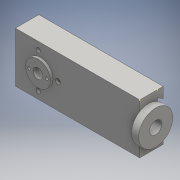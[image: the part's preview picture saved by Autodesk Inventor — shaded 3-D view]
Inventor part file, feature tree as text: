
AUTODESK INVENTOR PART (.ipt)
format: ipt  version: 2016 (Build 200138000, 138)  size: 212,480 bytes
history: native  units: mm
features: sketch x12, extrude x10
ambient origin geometry x8: Origin, YZ Plane, XZ Plane, XY Plane, X Axis, Y Axis, Z Axis, Center Point
bodies: Solid1 (feature_tree)
feature tree (22):
  extrude  "Extrusion1"  Depth=41.4mm
  extrude  "Extrusion2"  Depth=220.0mm
  extrude  "Extrusion3"  Depth=10.2mm
  sketch  "Sketch4"  dims[d7=65.0mm d8=19.0mm]
  extrude  "Extrusion4"  Depth=19.0mm
  sketch  "Sketch6"  dims[d13=15.1mm d14=141.9mm]
  extrude  "Extrusion5"  Depth=15.1mm
  extrude  "Extrusion6"  Depth=141.9mm
  extrude  "Extrusion7"  Depth=26.9mm
  extrude  "Extrusion8"  Depth=4.6mm
  extrude  "Extrusion9"  Depth=11.0mm TaperAngle=0.0deg
  extrude  "Extrusion10"  Depth=12.7mm TaperAngle=0.0deg
  sketch  "Sketch1"  dims[d0=89.0mm d1=41.4mm]
  sketch  "Sketch2"  dims[d2=220.0mm d3=0.0mm d4=18.6mm]
  sketch  "Sketch3"  dims[d5=10.2mm d6=12.5mm]
  sketch  "Sketch5"  dims[d9=301.25mm d10=0.0mm d12=15.1mm]
  sketch  "Sketch7"  dims[d15=26.9mm d16=0.0mm d17=28.6mm]
  sketch  "Sketch8"  dims[d18=30.2mm d19=4.6mm]
  sketch  "Sketch9"  dims[d21=11.0mm d22=91.9mm d23=0.0mm]
  sketch  "Sketch10"  dims[d24=60.4mm d25=12.7mm d26=0.0mm]
  sketch  "Sketch11"  dims[d27=10.6mm]
  sketch  "Sketch12"  dims[d28=83.6mm d29=90.0deg d30=4.9mm d31=6.0mm d32=0.0mm d33=22.0mm d34=22.3mm d35=22.7mm d36=22.15mm d37=0.0mm d38=4.6mm d39=0.0mm d40=17.5mm d41=310.85mm d42=0.0mm d43=4.4mm d44=5.0mm d45=4.4mm d46=2.5mm d47=3.5mm d48=0.0mm d49=40.7mm d50=9.4mm d51=4.0mm d52=40.7mm d53=9.4mm d54=4.0mm d55=70.6mm d56=39.5mm d57=4.5mm d58=4.5mm d59=7.0mm d60=0.0mm]
